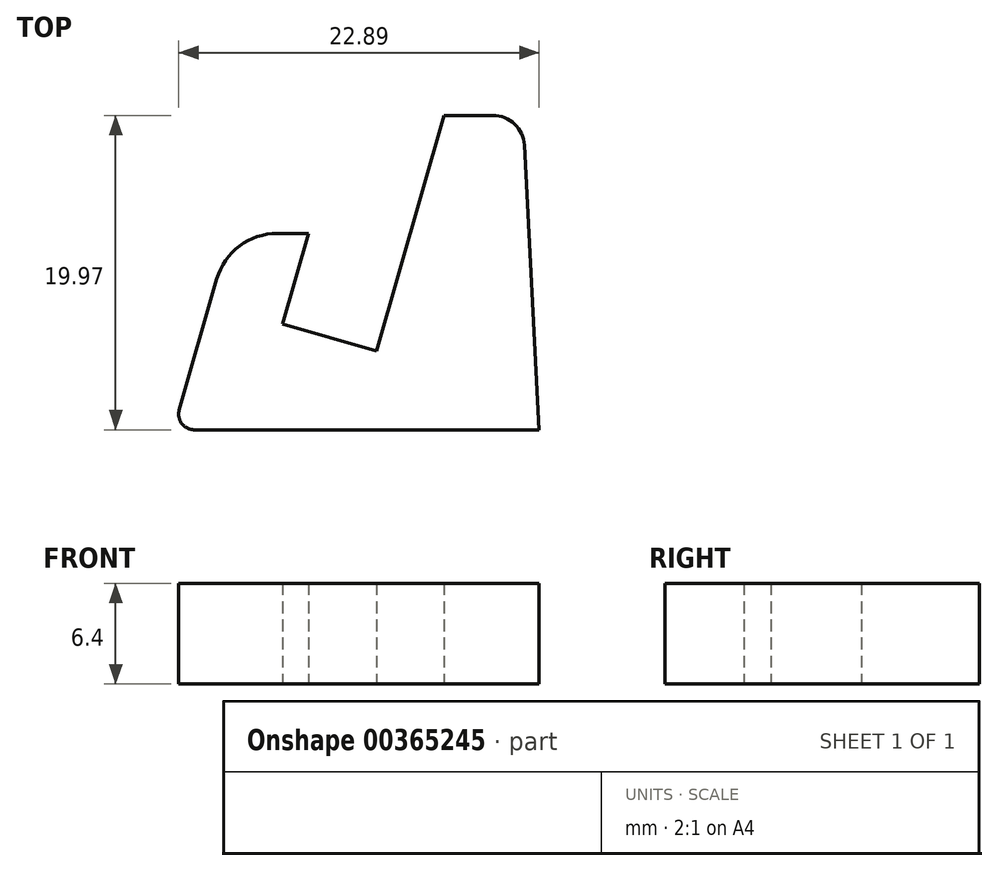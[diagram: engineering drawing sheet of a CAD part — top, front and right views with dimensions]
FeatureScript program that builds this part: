
annotation { "Feature Type Name" : "Feature", "Feature Type Description" : "" }
export const myFeature = defineFeature(function(context is Context, id is Id, definition is map)
    precondition{}
    {
        {
            var Q0;
            Q0=qCreatedBy(makeId("Top.planeOp"),FACE);
            var sketch = newSketch(context, id + "F0", { "sketchPlane" : qUnion([Q0])});
            skLineSegment(sketch, "E0", {"start": v(23.22, 0) * mm, "end": v(22.28, 18.08) * mm});
            skLineSegment(sketch, "E1", {"start": v(20.28, 19.97) * mm, "end": v(17.18, 19.97) * mm});
            skLineSegment(sketch, "E2", {"start": v(17.18, 19.97) * mm, "end": v(12.88, 5) * mm});
            skLineSegment(sketch, "E3", {"start": v(12.88, 5) * mm, "end": v(6.92, 6.7) * mm});
            skLineSegment(sketch, "E4", {"start": v(6.92, 6.7) * mm, "end": v(8.58, 12.48) * mm});
            skLineSegment(sketch, "E5", {"start": v(8.58, 12.48) * mm, "end": v(6.6, 12.48) * mm});
            skLineSegment(sketch, "E6", {"start": v(2.75, 9.58) * mm, "end": v(0.37, 1.28) * mm});
            skLineSegment(sketch, "E7", {"start": v(1.33, 0) * mm, "end": v(23.22, 0) * mm});
            skPoint(sketch, "E8.visualSharp", {"position": v(3.58, 12.48) * mm});
            skArc(sketch, "E8.filletArc", {"start": v(6.6, 12.48) * mm, "mid": v(4.18, 11.67) * mm, "end": v(2.75, 9.58) * mm});
            skPoint(sketch, "E9.visualSharp", {"position": v(0, 0) * mm});
            skArc(sketch, "E9.filletArc", {"start": v(0.37, 1.28) * mm, "mid": v(0.53, 0.4) * mm, "end": v(1.33, 0) * mm});
            skPoint(sketch, "E10.visualSharp", {"position": v(22.18, 19.97) * mm});
            skArc(sketch, "E10.filletArc", {"start": v(22.28, 18.08) * mm, "mid": v(21.66, 19.42) * mm, "end": v(20.28, 19.97) * mm});
            skSolve(sketch);
        }
        {
            var Q0;
            Q0 = qSketchRegion(id + "F0", true);
            extrude(context, id + "F1", {"entities" : qUnion([Q0]), "depth" : 6.4 * mm});
        }
    });
